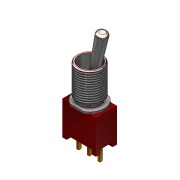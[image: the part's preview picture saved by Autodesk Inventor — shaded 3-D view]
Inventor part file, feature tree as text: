
AUTODESK INVENTOR PART (.ipt)
format: ipt  version: 2015 SP1 (Build 190203100, 203)  size: 269,312 bytes
history: native  units: mm
features: sketch x9, extrude x7, fillet x3, chamfer x2, thread x1, plane x1, sweep x1
ambient origin geometry x8: Origin, YZ Plane, XZ Plane, XY Plane, X Axis, Y Axis, Z Axis, Center Point
bodies: Volumenkörper1 (feature_tree)
feature tree (24):
  extrude  "Extrusion1"  Depth=5.0mm
  extrude  "Extrusion2"  Depth=7.0mm
  extrude  "Extrusion3"  Depth=0.5mm TaperAngle=0.0deg
  extrude  "Extrusion4"  Depth=1.0mm TaperAngle=0.0deg
  thread  "Gewinde1"  [1 undecoded]
  extrude  "Extrusion5"  Depth=10.0mm TaperAngle=0.0deg
  chamfer  "Fase1"  Distance=4.0mm
  chamfer  "Fase2"  Distance=0.2mm Angle=45.0deg
  extrude  "Extrusion6"  Depth=1.0mm
  extrude  "Extrusion7"  Depth=0.8mm
  fillet  "Rundung1"  Radius=0.4mm
  fillet  "Rundung2"  Radius=2.54mm
  sketch  "Skizze8"  dims[d26=1.0mm d27=0.0mm d28=0.8mm d29=0.4mm d30=2.54mm]
  plane  "Arbeitsebene1"
  sweep  "Sweeping1"
  fillet  "Rundung3"  Radius=0.3mm
  sketch  "Skizze1"  dims[d0=8.0mm d1=5.0mm]
  sketch  "Skizze2"  dims[d2=8.0mm d3=0.0mm d4=7.0mm]
  sketch  "Skizze3"  dims[d5=6.2mm d6=0.5mm d7=0.0mm]
  sketch  "Skizze4"  dims[d8=5.0mm d9=1.0mm d10=0.0mm d11=6.0mm]
  sketch  "Skizze5"  dims[d12=7.0mm d13=0.0mm d14=10.0mm d15=0.0mm]
  sketch  "Skizze6"  dims[d16=5.0mm d17=4.0mm d18=0.0mm d19=0.2mm d20=2.0mm d21=45.0deg]
  sketch  "Skizze7"  dims[d22=0.05mm d23=2.0mm d24=45.0deg d25=1.0mm]
  sketch  "Skizze9"  dims[d31=2.54mm d32=4.0mm d33=0.0mm d34=0.3mm d35=0.05mm d36=16.0mm d37=1.0mm d38=2.5mm d39=-0.349066mm d40=0.0mm d41=0.6mm]
note: 1 required parameter value undecoded (feature->parameter linkage not recoverable at this tier; creation-order binding heuristic only, values carry confidence <= 0.55)
